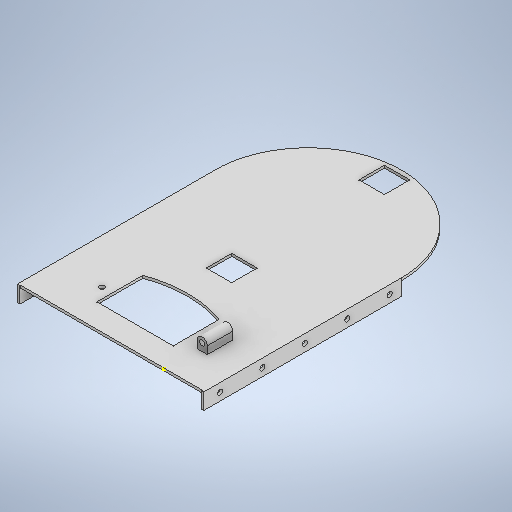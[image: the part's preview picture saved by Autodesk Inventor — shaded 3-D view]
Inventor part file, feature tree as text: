
AUTODESK INVENTOR PART (.ipt)
format: ipt  version: 2025.1 (Build 291241000, 241)  size: 344,576 bytes
history: native  units: mm
features: sketch x10, extrude x7, hole x2, mirror x1, plane x1, projected_geometry x1
ambient origin geometry x8: Origin, YZ Plane, XZ Plane, XY Plane, X Axis, Y Axis, Z Axis, Center Point
bodies: Solid1 (feature_tree)
feature tree (22):
  extrude  "Extrusion1"  Depth=116.0mm
  extrude  "Extrusion2"  Depth=65.0mm
  extrude  "Extrusion3"  Depth=14.0mm
  extrude  "Extrusion4"  Depth=1.5mm TaperAngle=0.0deg
  hole  "Hole1"  [1 undecoded]
  mirror  "Mirror1"
  plane  "Work Plane1"
  sketch  "Sketch8"  dims[d12=15.0mm d13=15.0mm]
  extrude  "Extrusion5"  Depth=15.0mm
  extrude  "Extrusion6"  Depth=37.5mm
  hole  "Hole2"  [1 undecoded]
  extrude  "Extrusion7"  Depth=9.5mm
  sketch  "Sketch2"  dims[d0=55.0mm d1=116.0mm]
  sketch  "Sketch3"  dims[d2=1.5mm d3=0.0mm d4=65.0mm]
  sketch  "Sketch4"  dims[d5=45.0mm d6=14.0mm]
  sketch  "Sketch6"  dims[d7=31.0mm d8=1.5mm d9=0.0mm]
  sketch  "Sketch7"  dims[d10=15.0mm d11=15.0mm]
  sketch  "Sketch9"  dims[d14=37.5mm d15=37.5mm]
  sketch  "Sketch10"  dims[d16=10.0mm d17=0.0mm d18=9.5mm]
  projected_geometry  "Projected Loop1"
  sketch  "Sketch11"  dims[d19=1.5mm d20=0.0mm d21=9.5mm]
  sketch  "Sketch12"  dims[d22=25.0mm d23=25.0mm d24=25.0mm d25=25.0mm d26=5.0mm d27=3.0mm d28=6.0mm d29=4.0mm d30=2.0mm d31=90.0deg d32=8.0mm d33=0.0mm d34=31.0mm d35=20.0mm d36=15.0mm d37=4.5mm d38=6.0mm d39=0.0mm d40=0.0mm d41=0.0mm d42=3.0mm d43=6.0mm d44=4.0mm d45=2.0mm d46=90.0deg d47=8.0mm d48=0.0mm d49=3.0mm d50=6.0mm d51=23.0mm d52=10.0mm d53=0.0mm]
note: 2 required parameter values undecoded (feature->parameter linkage not recoverable at this tier; creation-order binding heuristic only, values carry confidence <= 0.55)
